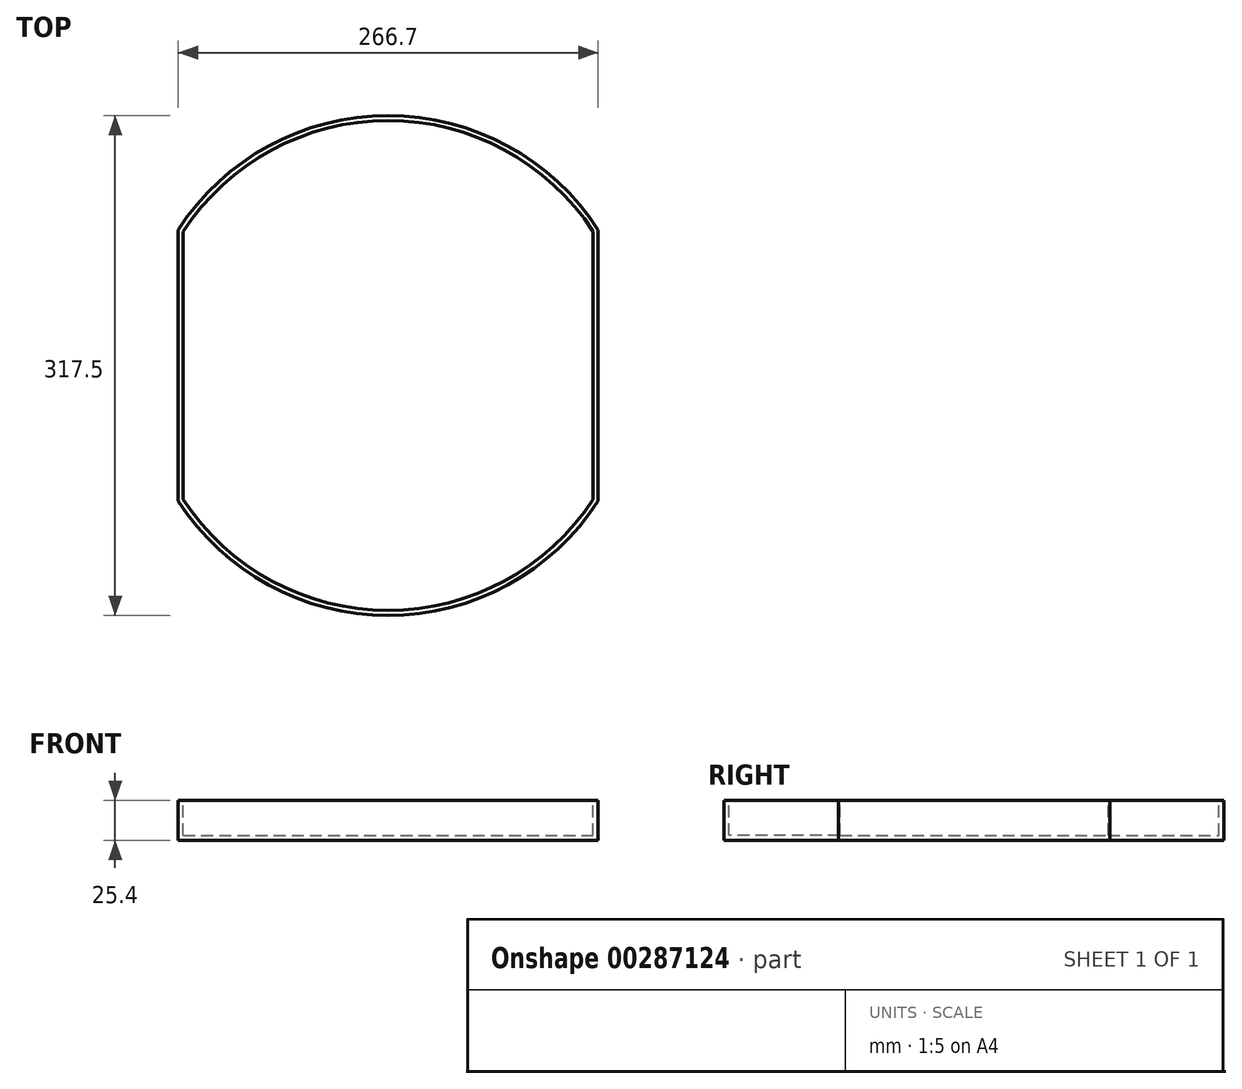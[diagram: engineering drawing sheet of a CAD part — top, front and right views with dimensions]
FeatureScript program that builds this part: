
annotation { "Feature Type Name" : "Feature", "Feature Type Description" : "" }
export const myFeature = defineFeature(function(context is Context, id is Id, definition is map)
    precondition{}
    {
        {
            var Q0;
            Q0=qCreatedBy(makeId("Top.planeOp"),FACE);
            var sketch = newSketch(context, id + "F0", { "sketchPlane" : qUnion([Q0])});
            skArc(sketch, "E0", {"start": v(-133.35, -86.14) * mm, "mid": v(0, -158.75) * mm, "end": v(133.35, -86.14) * mm});
            skLineSegment(sketch, "E1.left", {"start": v(133.35, -86.14) * mm, "end": v(133.35, 86.14) * mm});
            skLineSegment(sketch, "E1.right", {"start": v(-133.35, -86.14) * mm, "end": v(-133.35, 86.14) * mm});
            skArc(sketch, "E2.trimOffspring", {"start": v(133.35, 86.14) * mm, "mid": v(0, 158.75) * mm, "end": v(-133.35, 86.14) * mm});
            skSolve(sketch);
        }
        {
            var Q0;
            Q0=makeQuery(id+"F0.imprint","IMPRINT",FACE,{"disambiguationData":[TD([[makeQuery(id+"F0.imprint","IMPRINT",EDGE,{"derivedFrom":sQuery(id+"F0.wireOp",EDGE,"E0")}),1.0]])]});
            extrude(context, id + "F1", {"entities" : qUnion([Q0]), "oppositeDirection" : true, "depth" : 25.4 * mm});
        }
        {
            var Q0;
            Q0=makeQuery(id+"F1.opExtrude","CAP_FACE",FACE,{"disambiguationData":[OSD([sQuery(id+"F0.wireOp",EDGE,"E0"),sQuery(id+"F0.wireOp",EDGE,"E1.left"),sQuery(id+"F0.wireOp",EDGE,"E1.right"),sQuery(id+"F0.wireOp",EDGE,"E2.trimOffspring")])],"isStart":true});
            shell(context, id + "F2", {"entities" : qUnion([Q0]), "thickness" : 3.17 * mm});
        }
    });
